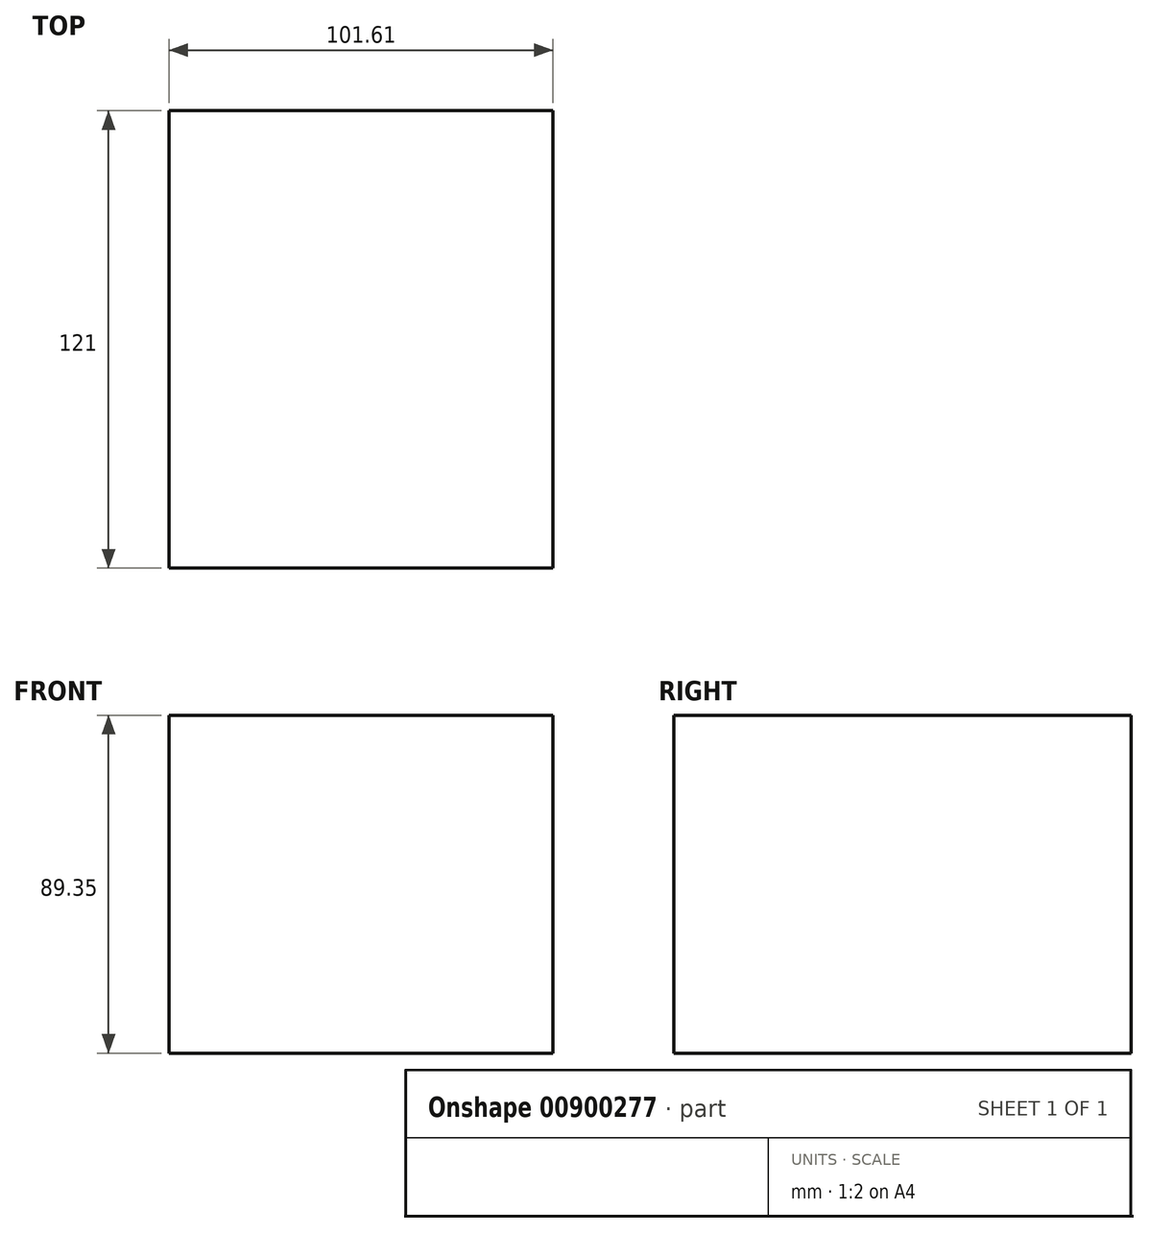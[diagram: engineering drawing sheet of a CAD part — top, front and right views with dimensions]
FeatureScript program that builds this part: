
annotation { "Feature Type Name" : "Feature", "Feature Type Description" : "" }
export const myFeature = defineFeature(function(context is Context, id is Id, definition is map)
    precondition{}
    {
        {
            var Q0;
            Q0=qCreatedBy(makeId("Front.planeOp"),FACE);
            var sketch = newSketch(context, id + "F0", { "sketchPlane" : qUnion([Q0])});
            skLineSegment(sketch, "E0.bottom", {"start": v(-63.1, 49.08) * mm, "end": v(38.51, 49.08) * mm});
            skLineSegment(sketch, "E0.top", {"start": v(-63.1, -40.27) * mm, "end": v(38.51, -40.27) * mm});
            skLineSegment(sketch, "E0.left", {"start": v(-63.1, 49.08) * mm, "end": v(-63.1, -40.27) * mm});
            skLineSegment(sketch, "E0.right", {"start": v(38.51, 49.08) * mm, "end": v(38.51, -40.27) * mm});
            skSolve(sketch);
        }
        {
            var Q0;
            Q0=makeQuery(id+"F0.imprint","IMPRINT",FACE,{"disambiguationData":[TD([[makeQuery(id+"F0.imprint","IMPRINT",EDGE,{"derivedFrom":sQuery(id+"F0.wireOp",EDGE,"E0.bottom")}),-1.0]])]});
            extrude(context, id + "F1", {"entities" : qUnion([Q0]), "depth" : 121 * mm, "offsetDistance" : 25 * mm});
        }
    });
